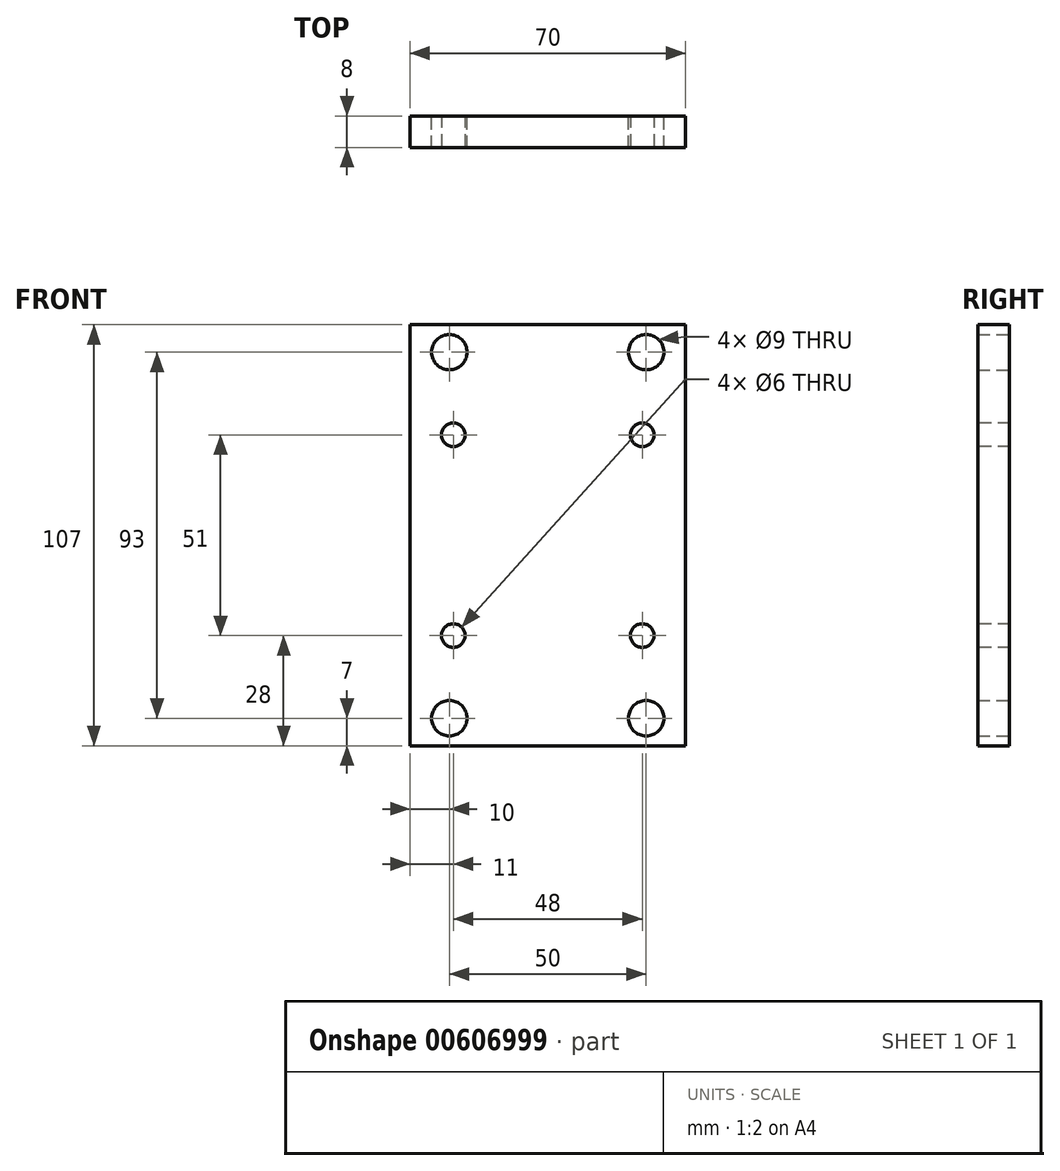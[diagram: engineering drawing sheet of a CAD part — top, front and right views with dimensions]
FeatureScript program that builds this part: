
annotation { "Feature Type Name" : "Feature", "Feature Type Description" : "" }
export const myFeature = defineFeature(function(context is Context, id is Id, definition is map)
    precondition{}
    {
        {
            var Q0;
            Q0=qCreatedBy(makeId("Front.planeOp"),FACE);
            var sketch = newSketch(context, id + "F0", { "sketchPlane" : qUnion([Q0]) });
            skLineSegment(sketch, "E0.bottom", {"start": v(35, 53.5) * mm, "end": v(-35, 53.5) * mm});
            skLineSegment(sketch, "E0.top", {"start": v(35, -53.5) * mm, "end": v(-35, -53.5) * mm});
            skLineSegment(sketch, "E0.left", {"start": v(35, 53.5) * mm, "end": v(35, -53.5) * mm});
            skLineSegment(sketch, "E0.right", {"start": v(-35, 53.5) * mm, "end": v(-35, -53.5) * mm});
            skPoint(sketch, "E0.middle", {"position": v(0, 0) * mm});
            skCircle(sketch, "E1", {"center": v(-25, 46.5) * mm, "radius": 4.5 * mm});
            skCircle(sketch, "E2.MirrorC", {"center": v(25, 46.5) * mm, "radius": 4.5 * mm});
            skCircle(sketch, "E3.MirrorC", {"center": v(-25, -46.5) * mm, "radius": 4.5 * mm});
            skCircle(sketch, "E4.MirrorC", {"center": v(25, -46.5) * mm, "radius": 4.5 * mm});
            skSolve(sketch);
        }
        {
            var Q0;
            Q0=makeQuery(id+"F0.imprint","IMPRINT",FACE,{"disambiguationData":[TD([[makeQuery(id+"F0.imprint","IMPRINT",EDGE,{"derivedFrom":sQuery(id+"F0.wireOp",EDGE,"E0.bottom")}),1.0]])]});
            extrude(context, id + "F1", {"entities" : qUnion([Q0]), "depth" : 8 * mm, "offsetDistance" : 25 * mm});
        }
        {
            var Q0;
            Q0=makeQuery(id+"F1.opExtrude","CAP_FACE",FACE,{"disambiguationData":[OSD([sQuery(id+"F0.wireOp",EDGE,"E0.bottom"),sQuery(id+"F0.wireOp",EDGE,"E0.top"),sQuery(id+"F0.wireOp",EDGE,"E0.left"),sQuery(id+"F0.wireOp",EDGE,"E0.right"),sQuery(id+"F0.wireOp",EDGE,"E1"),sQuery(id+"F0.wireOp",EDGE,"E2.MirrorC"),sQuery(id+"F0.wireOp",EDGE,"E3.MirrorC"),sQuery(id+"F0.wireOp",EDGE,"E4.MirrorC")])],"isStart":false});
            var sketch = newSketch(context, id + "F2", { "sketchPlane" : qUnion([Q0]) });
            skLineSegment(sketch, "E5.bottom", {"start": v(24, 25.5) * mm, "end": v(-24, 25.5) * mm});
            skLineSegment(sketch, "E5.top", {"start": v(24, -25.5) * mm, "end": v(-24, -25.5) * mm});
            skLineSegment(sketch, "E5.left", {"start": v(24, 25.5) * mm, "end": v(24, -25.5) * mm});
            skLineSegment(sketch, "E5.right", {"start": v(-24, 25.5) * mm, "end": v(-24, -25.5) * mm});
            skPoint(sketch, "E5.middle", {"position": v(0, 0) * mm});
            skPoint(sketch, "E6", {"position": v(-24, 25.5) * mm});
            skPoint(sketch, "E7", {"position": v(24, 25.5) * mm});
            skPoint(sketch, "E8", {"position": v(-24, -25.5) * mm});
            skPoint(sketch, "E9", {"position": v(24, -25.5) * mm});
            skSolve(sketch);
        }
        {
            var Q0;
            Q0=sQuery(id+"F2.wireOp",VERTEX,"E5.bottom.end");
            var Q1;
            Q1=sQuery(id+"F2.wireOp",VERTEX,"E7");
            var Q2;
            Q2=sQuery(id+"F2.wireOp",VERTEX,"E8");
            var Q3;
            Q3=sQuery(id+"F2.wireOp",VERTEX,"E9");
            var Q4;
            Q4=makeQuery(id+"F1.opExtrude","SWEPT_BODY",BODY,{"disambiguationData":[OSD([sQuery(id+"F0.wireOp",EDGE,"E0.bottom"),sQuery(id+"F0.wireOp",EDGE,"E0.top"),sQuery(id+"F0.wireOp",EDGE,"E0.left"),sQuery(id+"F0.wireOp",EDGE,"E0.right"),sQuery(id+"F0.wireOp",EDGE,"E1"),sQuery(id+"F0.wireOp",EDGE,"E2.MirrorC"),sQuery(id+"F0.wireOp",EDGE,"E3.MirrorC"),sQuery(id+"F0.wireOp",EDGE,"E4.MirrorC")])]});
            hole(context, id + "F3", {"style" : HoleStyle.SIMPLE, "endStyle" : HoleEndStyle.BLIND, "holeDiameter" : 6 * mm, "majorDiameter" : 5 * mm, "holeDepth" : 21 * mm, "tappedDepth" : 12.6 * mm, "tapClearance" : 3, "startFromSketch" : true, "locations" : qUnion([Q0, Q1, Q2, Q3]), "scope" : qUnion([Q4])});
        }
    });
